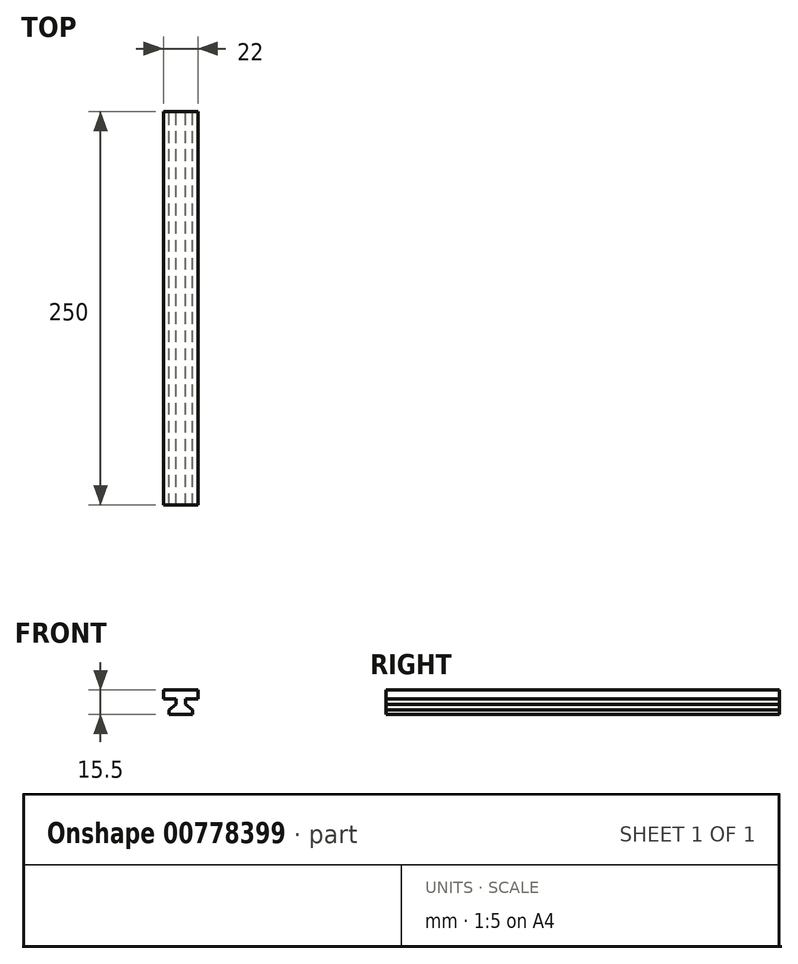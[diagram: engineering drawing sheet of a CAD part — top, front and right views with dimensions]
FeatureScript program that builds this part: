
annotation { "Feature Type Name" : "Feature", "Feature Type Description" : "" }
export const myFeature = defineFeature(function(context is Context, id is Id, definition is map)
    precondition{}
    {
        {
            var Q0;
            Q0=qCreatedBy(makeId("Front.planeOp"),FACE);
            var sketch = newSketch(context, id + "F0", { "sketchPlane" : qUnion([Q0])});
            skLineSegment(sketch, "E0.bottom", {"start": v(7.5, 0) * mm, "end": v(-7.5, 0) * mm});
            skLineSegment(sketch, "E0.top", {"start": v(7.5, 3) * mm, "end": v(-7.5, 3) * mm});
            skLineSegment(sketch, "E0.left", {"start": v(7.5, 0) * mm, "end": v(7.5, 3) * mm});
            skLineSegment(sketch, "E0.right", {"start": v(-7.5, 0) * mm, "end": v(-7.5, 3) * mm});
            skLineSegment(sketch, "E1", {"start": v(0, 0) * mm, "end": v(0, 10) * mm});
            skLineSegment(sketch, "E2", {"start": v(0, 10) * mm, "end": v(0, 15.5) * mm});
            skLineSegment(sketch, "E3", {"start": v(-11, 15.5) * mm, "end": v(11, 15.5) * mm});
            skLineSegment(sketch, "E4", {"start": v(-11, 10) * mm, "end": v(11, 10) * mm});
            skLineSegment(sketch, "E5", {"start": v(-11, 15.5) * mm, "end": v(-11, 10) * mm});
            skLineSegment(sketch, "E6", {"start": v(11, 15.5) * mm, "end": v(11, 10) * mm});
            skLineSegment(sketch, "E7.bottom", {"start": v(-3, 10) * mm, "end": v(3, 10) * mm});
            skLineSegment(sketch, "E7.top", {"start": v(-3, 3) * mm, "end": v(3, 3) * mm});
            skLineSegment(sketch, "E7.left", {"start": v(-3, 10) * mm, "end": v(-3, 3) * mm});
            skLineSegment(sketch, "E7.right", {"start": v(3, 10) * mm, "end": v(3, 3) * mm});
            skPoint(sketch, "E8", {"position": v(-3, 6.5) * mm});
            skPoint(sketch, "E9", {"position": v(3, 6.5) * mm});
            skLineSegment(sketch, "E10", {"start": v(-3, 6.5) * mm, "end": v(-7.5, 3) * mm});
            skLineSegment(sketch, "E11", {"start": v(3, 6.5) * mm, "end": v(7.5, 3) * mm});
            skSolve(sketch);
        }
        {
            var Q0;
            {var subQ0=sQuery(id+"F0.wireOp",EDGE,"E11");Q0=makeQuery(id+"F0.imprint","IMPRINT",FACE,{"disambiguationData":[TD([[makeQuery(id+"F0.imprint","IMPRINT",EDGE,{"derivedFrom":subQ0}),-1.0]])]});}
            var Q1;
            {var subQ0=sQuery(id+"F0.wireOp",EDGE,"E10");Q1=makeQuery(id+"F0.imprint","IMPRINT",FACE,{"disambiguationData":[TD([[makeQuery(id+"F0.imprint","IMPRINT",EDGE,{"derivedFrom":subQ0}),1.0]])]});}
            var Q2;
            {var subQ5=sQuery(id+"F0.wireOp",EDGE,"E2");Q2=makeQuery(id+"F0.imprint","IMPRINT",FACE,{"disambiguationData":[TD([[makeQuery(id+"F0.imprint","IMPRINT",EDGE,{"derivedFrom":subQ5}),1.0]])]});}
            var Q3;
            {var subQ5=sQuery(id+"F0.wireOp",EDGE,"E2");Q3=makeQuery(id+"F0.imprint","IMPRINT",FACE,{"disambiguationData":[TD([[makeQuery(id+"F0.imprint","IMPRINT",EDGE,{"derivedFrom":subQ5}),-1.0]])]});}
            var Q4;
            {var subQ5=sQuery(id+"F0.wireOp",EDGE,"E0.left");Q4=makeQuery(id+"F0.imprint","IMPRINT",FACE,{"disambiguationData":[TD([[makeQuery(id+"F0.imprint","IMPRINT",EDGE,{"derivedFrom":subQ5}),1.0]])]});}
            var Q5;
            {var subQ0=sQuery(id+"F0.wireOp",EDGE,"E0.right");Q5=makeQuery(id+"F0.imprint","IMPRINT",FACE,{"disambiguationData":[TD([[makeQuery(id+"F0.imprint","IMPRINT",EDGE,{"derivedFrom":subQ0}),-1.0]])]});}
            var Q6;
            {var subQ4=sQuery(id+"F0.wireOp",EDGE,"E1");var subQ6=sQuery(id+"F0.wireOp",EDGE,"E7.top");var subQ8=makeQuery(id+"F0.imprint","INTERSECT",VERTEX,{"derivedFrom":[subQ4,subQ6]});Q6=makeQuery(id+"F0.imprint","IMPRINT",FACE,{"disambiguationData":[TD([[makeQuery(id+"F0.imprint","IMPRINT",EDGE,{"disambiguationData":[TD([[subQ8,-1.0]])],"derivedFrom":subQ4}),1.0]])]});}
            var Q7;
            {var subQ1=sQuery(id+"F0.wireOp",EDGE,"E7.top");var subQ3=sQuery(id+"F0.wireOp",EDGE,"E1");var subQ4=makeQuery(id+"F0.imprint","INTERSECT",VERTEX,{"derivedFrom":[subQ3,subQ1]});Q7=makeQuery(id+"F0.imprint","IMPRINT",FACE,{"disambiguationData":[TD([[makeQuery(id+"F0.imprint","IMPRINT",EDGE,{"disambiguationData":[TD([[subQ4,-1.0]])],"derivedFrom":subQ3}),-1.0]])]});}
            extrude(context, id + "F1", {"entities" : qUnion([Q0, Q1, Q2, Q3, Q4, Q5, Q6, Q7]), "depth" : 250 * mm, "offsetDistance" : 25 * mm});
        }
    });
